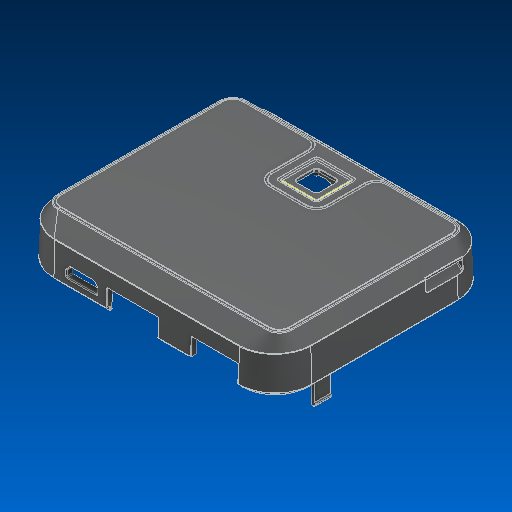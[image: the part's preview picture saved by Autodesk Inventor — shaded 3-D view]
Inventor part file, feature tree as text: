
AUTODESK INVENTOR PART (.ipt)
format: ipt  version: 2022.2 (Build 262287000, 287)  size: 3,319,808 bytes
history: native  units: in
note: dims shown in document units (in); Inventor stores cm internally (conversion verified against a paired STEP export)
features: chamfer x1
ambient origin geometry x8: Origin, YZ Plane, XZ Plane, XY Plane, X Axis, Y Axis, Z Axis, Center Point
bodies: Solid1 (feature_tree)
feature tree (1):
  chamfer  "Chamfer4"  [1 undecoded]
note: 1 required parameter value undecoded (feature->parameter linkage not recoverable at this tier; creation-order binding heuristic only, values carry confidence <= 0.55)
